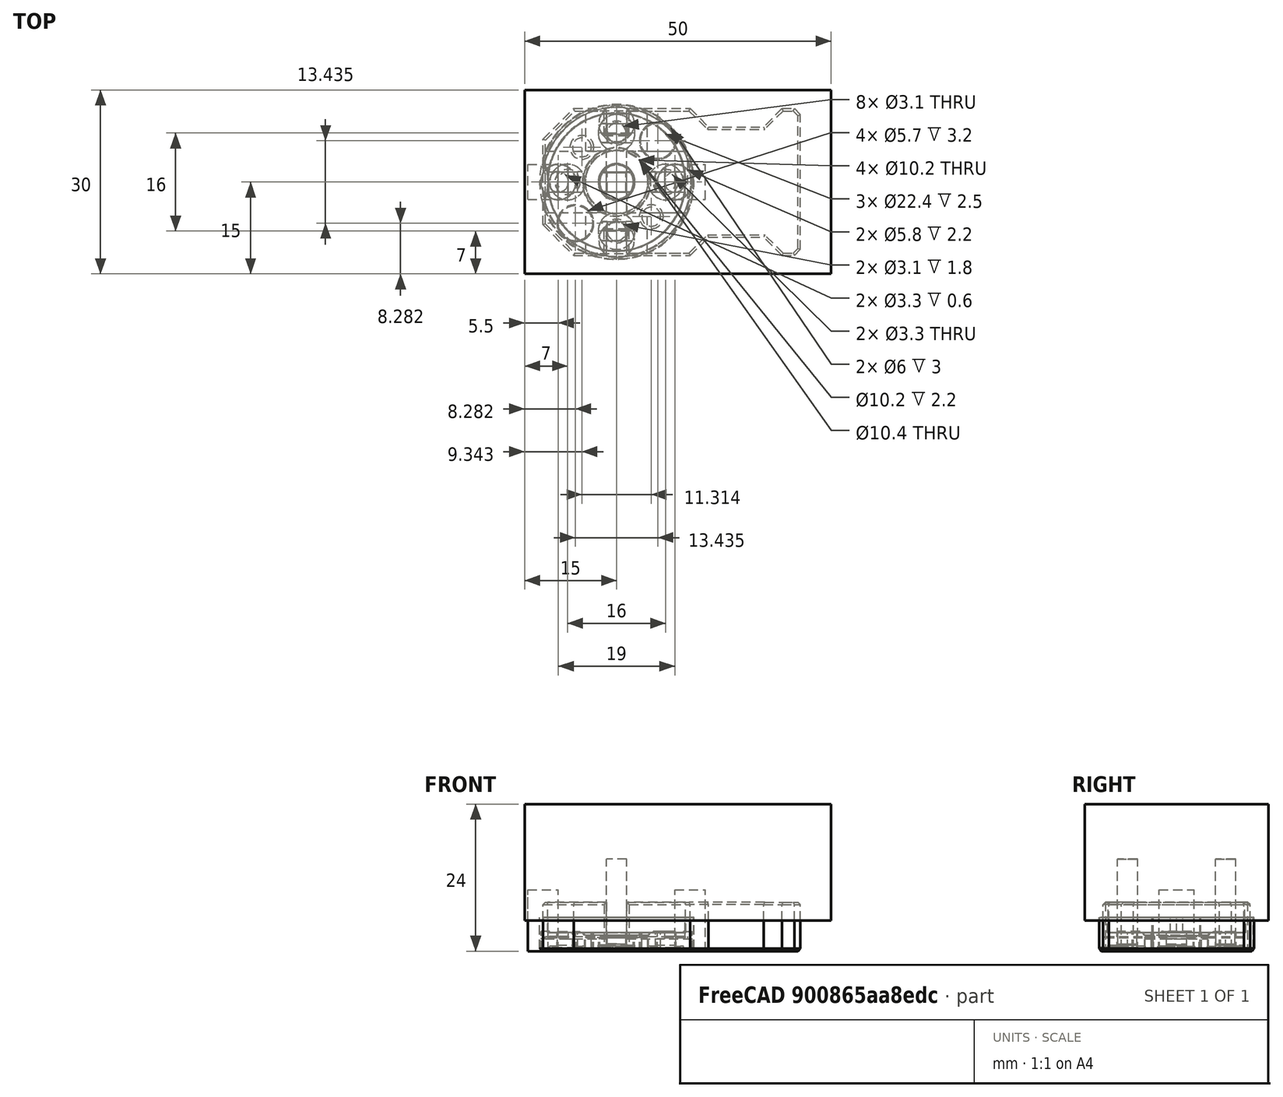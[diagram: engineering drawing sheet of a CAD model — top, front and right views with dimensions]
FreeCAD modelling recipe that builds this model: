
FCSTD DOCUMENT  (FreeCAD 0.18R14555 (Git shallow))
Label: fucking-leadscrew-nut-adapter
License: All rights reserved
LicenseURL: http://en.wikipedia.org/wiki/All_rights_reserved
objects: Part::Cylinder×26, Part::Feature×22, Part::Box×20, Part::Cut×16, Part::MultiFuse×11, Part::Chamfer×6, App::DocumentObjectGroup×1
note: 101 computed .brp shape members not serialized (recipe doc carries the construction recipe); baked Part::Feature solids carry a one-line shape summary decoded from their .brp

FEATURE [Part::Cylinder] Cylinder007
  Angle = 360
  AttacherType = Attacher::AttachEngine3D
  Height = 15
  Placement = pos=(0,-8,0) rot=(0,0,1;0rad)
  Radius = 1.65
FEATURE [Part::Cylinder] Cylinder008
  Angle = 360
  AttacherType = Attacher::AttachEngine3D
  Height = 15
  Placement = pos=(0,8,0) rot=(0,0,1;0rad)
  Radius = 1.65
FEATURE [Part::Cylinder] Cylinder009
  Angle = 360
  AttacherType = Attacher::AttachEngine3D
  Height = 10
  Radius = 5.2
FEATURE [Part::Cylinder] Cylinder010
  Angle = 360
  AttacherType = Attacher::AttachEngine3D
  Height = 10
  Placement = pos=(-8,0,0) rot=(0,0,1;0rad)
  Radius = 1.65
FEATURE [Part::Cylinder] Cylinder011
  Angle = 360
  AttacherType = Attacher::AttachEngine3D
  Height = 10
  Placement = pos=(8,0,0) rot=(0,0,1;0rad)
  Radius = 1.65
FEATURE [Part::Cylinder] Cylinder020
  Angle = 360
  AttacherType = Attacher::AttachEngine3D
  Height = 1
  Radius = 2.9
FEATURE [Part::Box] Box001  label="Cube001"
  AttacherType = Attacher::AttachEngine3D
  Height = 0.4
  Length = 10
  Placement = pos=(-5,1.65,0) rot=(0,0,1;0rad)
  Width = 10
FEATURE [Part::Box] Box002  label="Cube002"
  AttacherType = Attacher::AttachEngine3D
  Height = 0.4
  Length = 10
  Placement = pos=(-5,-11.65,0) rot=(0,0,1;0rad)
  Width = 10
FEATURE [Part::Box] Box003  label="Cube003"
  AttacherType = Attacher::AttachEngine3D
  Height = 0.2
  Length = 10
  Placement = pos=(1.65,-5,0.2) rot=(0,0,1;0rad)
  Width = 10
FEATURE [Part::Box] Box004  label="Cube004"
  AttacherType = Attacher::AttachEngine3D
  Height = 0.2
  Length = 10
  Placement = pos=(-11.65,-5,0.2) rot=(0,0,1;0rad)
  Width = 10
FEATURE [Part::MultiFuse] Fusion003
  Placement = pos=(0,0,0.6) rot=(0,0,1;0rad)
  Shapes = -> [Box004,Box002,Box003,Box001]
FEATURE [Part::Cut] Cut017
  Base = -> Cylinder020
  Tool = -> Fusion003
FEATURE [Part::Feature] Cut017001  label="Cut018"
  Placement = pos=(-8,0,0) rot=(0,0,1;0rad)
  shape: bbox 5.8 x 5.8 x 1 mm, 11 faces (baked)
FEATURE [Part::Feature] Cut017002  label="Cut019"
  Placement = pos=(8,0,0) rot=(0,0,1;0rad)
  shape: bbox 5.8 x 5.8 x 1 mm, 11 faces (baked)
FEATURE [Part::Feature] Cut017003  label="Cut020"
  Placement = pos=(0,9.5,0) rot=(0,0,1;0rad)
  shape: bbox 5.8 x 5.8 x 1 mm, 11 faces (baked)
FEATURE [Part::Feature] Cut017004  label="Cut021"
  Placement = pos=(0,-9.5,0) rot=(0,0,1;0rad)
  shape: bbox 5.8 x 5.8 x 1 mm, 11 faces (baked)
FEATURE [Part::MultiFuse] Fusion004
  Shapes = -> [Cut017001,Cut017004,Cut017002,Cut017003]
FEATURE [Part::Cylinder] Cylinder023
  Angle = 360
  AttacherType = Attacher::AttachEngine3D
  Height = 17
  Placement = pos=(0,0,3) rot=(0,0,1;0rad)
  Radius = 11.25
FEATURE [Part::Box] Box  label="Cube"
  AttacherType = Attacher::AttachEngine3D
  Height = 8
  Length = 42
  Placement = pos=(-12,-12,0) rot=(0,0,1;0rad)
  Width = 24
FEATURE [Part::Box] Box005  label="Cube005"
  AttacherType = Attacher::AttachEngine3D
  Height = 15
  Length = 3.3
  Placement = pos=(-1.65,-28,0) rot=(0,0,1;0rad)
  Width = 20
FEATURE [Part::Box] Box006  label="Cube006"
  AttacherType = Attacher::AttachEngine3D
  Height = 15
  Length = 3.3
  Placement = pos=(-1.65,8,0) rot=(0,0,1;0rad)
  Width = 20
FEATURE [Part::Box] Box007  label="Cube007"
  AttacherType = Attacher::AttachEngine3D
  Height = 20
  Length = 15
  Placement = pos=(15,12,0) rot=(0,0,1;0rad)
  Width = 4
FEATURE [Part::Box] Box008  label="Cube008"
  AttacherType = Attacher::AttachEngine3D
  Height = 20
  Length = 15
  Placement = pos=(15,-16,0) rot=(0,0,1;0rad)
  Width = 4
FEATURE [Part::Chamfer] Chamfer001
  Base = -> Box007
  Edges = 2 edges r=3: [Edge1,Edge5]
  Placement = pos=(-3,-3,0) rot=(0,0,1;0rad)
FEATURE [Part::Chamfer] Chamfer002
  Base = -> Box008
  Edges = 2 edges r=3: [Edge3,Edge7]
  Placement = pos=(-3,3,0) rot=(0,0,1;0rad)
FEATURE [Part::Cylinder] Cylinder024
  Angle = 360
  AttacherType = Attacher::AttachEngine3D
  Height = 5.5
  Radius = 12.65
FEATURE [Part::Cylinder] Cylinder025
  Angle = 360
  AttacherType = Attacher::AttachEngine3D
  Height = 5.5
  Placement = pos=(0,0,3) rot=(0,0,1;0rad)
  Radius = 11.3
FEATURE [Part::Cylinder] Cylinder026
  Angle = 360
  AttacherType = Attacher::AttachEngine3D
  Height = 10
  Radius = 5.1
FEATURE [Part::Cylinder] Cylinder027
  Angle = 360
  AttacherType = Attacher::AttachEngine3D
  Height = 5
  Placement = pos=(0,-8,0) rot=(0,0,1;0rad)
  Radius = 1.55
FEATURE [Part::Cylinder] Cylinder028
  Angle = 360
  AttacherType = Attacher::AttachEngine3D
  Height = 5
  Placement = pos=(0,8,0) rot=(0,0,1;0rad)
  Radius = 1.55
FEATURE [Part::Box] Box010  label="Cube010"
  AttacherType = Attacher::AttachEngine3D
  Height = 10
  Length = 5
  Placement = pos=(9.5,-2.85,0) rot=(0,0,1;0rad)
  Width = 5.7
FEATURE [Part::Box] Box011  label="Cube011"
  AttacherType = Attacher::AttachEngine3D
  Height = 10
  Length = 5
  Placement = pos=(-14.5,-2.85,0) rot=(0,0,1;0rad)
  Width = 5.7
FEATURE [Part::Cylinder] Cylinder031
  Angle = 360
  AttacherType = Attacher::AttachEngine3D
  Height = 3.2
  Placement = pos=(-9.5,0,0) rot=(0,0,1;0rad)
  Radius = 2.65
FEATURE [Part::Cylinder] Cylinder032
  Angle = 360
  AttacherType = Attacher::AttachEngine3D
  Height = 3.2
  Placement = pos=(9.5,0,0) rot=(0,0,1;0rad)
  Radius = 2.65
FEATURE [Part::Box] Box014  label="Cube014"
  AttacherType = Attacher::AttachEngine3D
  Height = 19
  Length = 50
  Placement = pos=(-15,-15,5) rot=(0,0,1;0rad)
  Width = 30
FEATURE [Part::MultiFuse] Fusion
  Shapes = -> [Cylinder008,Cylinder007]
FEATURE [Part::MultiFuse] Fusion014
  Shapes = -> [Chamfer002,Chamfer001,Box006,Box005,Cylinder009,Cylinder010,Cylinder011]
FEATURE [Part::Cut] Cut
  Base = -> Box
  Tool = -> Fusion014
FEATURE [Part::Cut] Cut017021004
  Base = -> Cut
  Tool = -> Cylinder023
FEATURE [Part::Chamfer] Chamfer
  Base = -> Cut017021004
  Edges = 2 edges r=5: [Edge1,Edge3]
FEATURE [Part::Chamfer] Chamfer008
  Base = -> Chamfer
  Edges = 2 edges r=1: [Edge69,Edge73]
FEATURE [Part::Chamfer] Chamfer009  label="supporter"
  Base = -> Chamfer008
  Edges = 50 edges r=0.4: [Edge1,Edge2,Edge3,Edge4,Edge5,Edge6,Edge7,Edge8,Edge9,Edge10,Edge11,Edge12,Edge13,Edge14,Edge15,Edge16,Edge17,Edge18,Edge19,Edge20,Edge21,Edge22,Edge23,Edge24,Edge25,Edge26,Edge27,Edge30,Edge32,Edge34,Edge35,Edge37,Edge40,Edge41,Edge44,Edge45,Edge46,Edge48,Edge53,Edge57,Edge62,Edge63,Edge64,Edge65,+6 more]
FEATURE [Part::MultiFuse] Fusion016  label="screw-hole-small"
  Shapes = -> [Cylinder032,Cylinder031]
FEATURE [Part::MultiFuse] Fusion017
  Shapes = -> [Cylinder028,Cylinder027]
FEATURE [Part::Feature] Chamfer010001  label="adapter-base-chamber001"
  shape: bbox 25.1 x 25.1 x 5.5 mm, 13 faces (baked)
FEATURE [Part::Feature] Chamfer010002  label="adapter-base-chamber002"
  shape: bbox 25.1 x 25.1 x 5.5 mm, 13 faces (baked)
FEATURE [Part::Cut] Cut017021010  label="adapter-small"
  Base = -> Chamfer010002
  Tool = -> Fusion016
FEATURE [Part::Cylinder] Cylinder
  Angle = 360
  AttacherType = Attacher::AttachEngine3D
  Height = 1.2
  Radius = 3
FEATURE [Part::Box] Box015  label="Cube015"
  AttacherType = Attacher::AttachEngine3D
  Height = 0.2
  Length = 10
  Placement = pos=(1.55,-5,0.2) rot=(0,0,1;0rad)
  Width = 10
FEATURE [Part::Box] Box016  label="Cube016"
  AttacherType = Attacher::AttachEngine3D
  Height = 0.2
  Length = 10
  Placement = pos=(-11.55,-5,0.2) rot=(0,0,1;0rad)
  Width = 10
FEATURE [Part::Box] Box017  label="Cube017"
  AttacherType = Attacher::AttachEngine3D
  Height = 0.4
  Length = 10
  Placement = pos=(-5,1.55,0) rot=(0,0,1;0rad)
  Width = 10
FEATURE [Part::Box] Box018  label="Cube018"
  AttacherType = Attacher::AttachEngine3D
  Height = 0.4
  Length = 10
  Placement = pos=(-5,-11.55,0) rot=(0,0,1;0rad)
  Width = 10
FEATURE [Part::MultiFuse] Fusion018
  Placement = pos=(0,0,0.8) rot=(0,0,1;0rad)
  Shapes = -> [Box016,Box018,Box015,Box017]
FEATURE [Part::Cut] Cut017021011  label="screw-rotate-locker-m3"
  Base = -> Cylinder
  Tool = -> Fusion018
FEATURE [Part::Feature] Cut017021010002  label="adapter-small-grub"
  shape: bbox 25.1 x 25.1 x 5.5 mm, 17 faces (baked)
FEATURE [Part::Feature] Cut017021008002  label="adapter-big-grub"
  shape: bbox 25.1 x 25.1 x 5.5 mm, 17 faces (baked)
FEATURE [App::DocumentObjectGroup] Group  label="Export"
  Group = -> [Cut017021008002,Cut017021010002]
FEATURE [Part::Box] Box019  label="Cube019"
  AttacherType = Attacher::AttachEngine3D
  Height = 0.2
  Length = 10
  Placement = pos=(-5,1.65,0.2) rot=(0,0,1;0rad)
  Width = 10
FEATURE [Part::Box] Box020  label="Cube020"
  AttacherType = Attacher::AttachEngine3D
  Height = 0.2
  Length = 10
  Placement = pos=(-5,-11.65,0.2) rot=(0,0,1;0rad)
  Width = 10
FEATURE [Part::Box] Box021  label="Cube021"
  AttacherType = Attacher::AttachEngine3D
  Height = 0.4
  Length = 10
  Placement = pos=(1.65,-5,0) rot=(0,0,1;0rad)
  Width = 10
FEATURE [Part::Box] Box022  label="Cube022"
  AttacherType = Attacher::AttachEngine3D
  Height = 0.4
  Length = 10
  Placement = pos=(-11.65,-5,0) rot=(0,0,1;0rad)
  Width = 10
FEATURE [Part::MultiFuse] Fusion021  label="165-sp"
  Placement = pos=(0,0,2) rot=(0,0,1;0rad)
  Shapes = -> [Box019,Box021,Box020,Box022]
FEATURE [Part::Cylinder] Cylinder033
  Angle = 360
  AttacherType = Attacher::AttachEngine3D
  Height = 2.4
  Radius = 2.75
FEATURE [Part::Feature] Fusion021001  label="165-sp001"
  Placement = pos=(0,0,2) rot=(0,0,1;0rad)
  shape: bbox 23.3 x 23.3 x 0.4 mm, 28 faces (baked)
FEATURE [Part::Cut] Cut017021010003  label="small-screw"
  Base = -> Cylinder033
  Tool = -> Fusion021001
FEATURE [Part::Feature] Fusion021002  label="165-sp002"
  Placement = pos=(0,0,2) rot=(0,0,1;0rad)
  shape: bbox 23.3 x 23.3 x 0.4 mm, 28 faces (baked)
FEATURE [Part::Cylinder] Cylinder034
  Angle = 360
  AttacherType = Attacher::AttachEngine3D
  Height = 2.4
  Radius = 2.9
FEATURE [Part::Cut] Cut017021010004  label="big-screw"
  Base = -> Cylinder034
  Tool = -> Fusion021002
FEATURE [Part::Feature] Chamfer010003  label="adapter-base-chamber003"
  shape: bbox 25.1 x 25.1 x 5.5 mm, 13 faces (baked)
FEATURE [Part::Feature] Cut017021010004001  label="big-screw001"
  Placement = pos=(9.5,0,0) rot=(0,0,1;0rad)
  shape: bbox 5.8 x 5.8 x 2.4 mm, 11 faces (baked)
FEATURE [Part::Feature] Cut017021010004002  label="big-screw002"
  Placement = pos=(-9.5,0,0) rot=(0,0,1;0rad)
  shape: bbox 5.8 x 5.8 x 2.4 mm, 11 faces (baked)
FEATURE [Part::Feature] Cut017021011001  label="screw-rotate-locker-m004"
  Placement = pos=(0,8,0) rot=(0,0,1;0rad)
  shape: bbox 6 x 6 x 1.2 mm, 11 faces (baked)
FEATURE [Part::Feature] Cut017021010004003  label="screw-rotate-locker-m005"
  Placement = pos=(0,-8,0) rot=(0,0,1;0rad)
  shape: bbox 6 x 6 x 1.2 mm, 11 faces (baked)
FEATURE [Part::Cylinder] Cylinder035
  Angle = 360
  AttacherType = Attacher::AttachEngine3D
  Height = 10
  Placement = pos=(-9.5,0,0) rot=(0,0,1;0rad)
  Radius = 1.65
FEATURE [Part::Cylinder] Cylinder036
  Angle = 360
  AttacherType = Attacher::AttachEngine3D
  Height = 10
  Placement = pos=(9.5,0,0) rot=(0,0,1;0rad)
  Radius = 1.65
FEATURE [Part::Cylinder] Cylinder037
  Angle = 360
  AttacherType = Attacher::AttachEngine3D
  Height = 10
  Placement = pos=(-9.5,0,0) rot=(0,0,1;0rad)
  Radius = 1.65
FEATURE [Part::Cylinder] Cylinder038
  Angle = 360
  AttacherType = Attacher::AttachEngine3D
  Height = 10
  Placement = pos=(9.5,0,0) rot=(0,0,1;0rad)
  Radius = 1.65
FEATURE [Part::Feature] Cut017021010004004  label="screw-rotate-locker-m006"
  Placement = pos=(0,8,0) rot=(0,0,1;0rad)
  shape: bbox 6 x 6 x 1.2 mm, 11 faces (baked)
FEATURE [Part::Feature] Cut017021010004005  label="screw-rotate-locker-m007"
  Placement = pos=(0,-8,0) rot=(0,0,1;0rad)
  shape: bbox 6 x 6 x 1.2 mm, 11 faces (baked)
FEATURE [Part::MultiFuse] Fusion021003
  Shapes = -> [Cut017021010004005,Cut017021010004004,Cylinder038,Cylinder037,Cut017021010004002,Cut017021010004001]
FEATURE [Part::Cut] Cut017021010004006  label="std-adapter-big"
  Base = -> Chamfer010003
  Tool = -> Fusion021003
FEATURE [Part::Feature] Cut017021010003001  label="small-screw001"
  Placement = pos=(9.5,0,0) rot=(0,0,1;0rad)
  shape: bbox 5.5 x 5.5 x 2.4 mm, 11 faces (baked)
FEATURE [Part::Feature] Cut017021010004007  label="small-screw002"
  Placement = pos=(-9.5,0,0) rot=(0,0,1;0rad)
  shape: bbox 5.5 x 5.5 x 2.4 mm, 11 faces (baked)
FEATURE [Part::MultiFuse] Fusion021004
  Shapes = -> [Cut017021010004007,Cut017021010003001,Cylinder036,Cylinder035,Cut017021010004003,Cut017021011001]
FEATURE [Part::Cut] Cut017021010004008  label="std-adapter-small"
  Base = -> Chamfer010001
  Tool = -> Fusion021004
FEATURE [Part::Feature] Cut017021010002001  label="adapter-small-grub001"
  Placement = pos=(0,0,0) rot=(0,0,1;0.785398rad)
  shape: bbox 25.1 x 25.1 x 5.5 mm, 17 faces (baked)
FEATURE [Part::Cylinder] Cylinder039
  Angle = 360
  AttacherType = Attacher::AttachEngine3D
  Height = 10
  Placement = pos=(-21.2,0,0) rot=(0,0,1;0rad)
  Radius = 10
FEATURE [Part::Cut] Cut017021010004009  label="adapter-small-grub-cutout"
  Base = -> Cut017021010002001
  Tool = -> Cylinder039
FEATURE [Part::Cylinder] Cylinder040
  Angle = 360
  AttacherType = Attacher::AttachEngine3D
  Height = 10
  Placement = pos=(-21.2,0,0) rot=(0,0,1;0rad)
  Radius = 10
FEATURE [Part::Feature] Cut017021010004010  label="adapter-big-grub001"
  Placement = pos=(0,0,0) rot=(0,0,1;0.785398rad)
  shape: bbox 25.1 x 25.1 x 5.5 mm, 17 faces (baked)
FEATURE [Part::Feature] Chamfer010004  label="adapter-base-chamber004"
  shape: bbox 25.1 x 25.1 x 5.5 mm, 13 faces (baked)
FEATURE [Part::Cut] Cut017021010004011  label="adapter-big-grub-cutout"
  Base = -> Cut017021010004010
  Tool = -> Cylinder040
FEATURE [Part::Cut] Cut017021010004012
  Base = -> Cylinder024
  Tool = -> Cylinder025
FEATURE [Part::Cut] Cut017021010004013
  Base = -> Cut017021010004012
  Tool = -> Cylinder026
FEATURE [Part::Cut] Cut017021010004014
  Base = -> Cut017021010004013
  Tool = -> Fusion017
FEATURE [Part::Cylinder] Cylinder041
  Angle = 360
  AttacherType = Attacher::AttachEngine3D
  Height = 3
  Placement = pos=(9.5,0,0) rot=(0,0,1;0rad)
  Radius = 3
FEATURE [Part::Cylinder] Cylinder042
  Angle = 360
  AttacherType = Attacher::AttachEngine3D
  Height = 3
  Placement = pos=(-9.5,0,0) rot=(0,0,1;0rad)
  Radius = 3
FEATURE [Part::Chamfer] Chamfer010005
  Base = -> Cut017021010004014
  Edges = 5 edges r=0.4: [Edge3,Edge5,Edge6,Edge7,Edge12]
FEATURE [Part::MultiFuse] Fusion021005
  Shapes = -> [Cylinder041,Cylinder042]
FEATURE [Part::Cylinder] Cylinder043
  Angle = 360
  AttacherType = Attacher::AttachEngine3D
  Height = 10
  Placement = pos=(-21.2,0,0) rot=(0,0,1;0rad)
  Radius = 10
FEATURE [Part::Cut] Cut017021010004015
  Base = -> Chamfer010005
  Placement = pos=(0,0,0) rot=(0,0,1;0.785398rad)
  Tool = -> Fusion021005
FEATURE [Part::Cut] Cut017021010004016  label="adapter-standard"
  Base = -> Cut017021010004015
  Tool = -> Cylinder043
